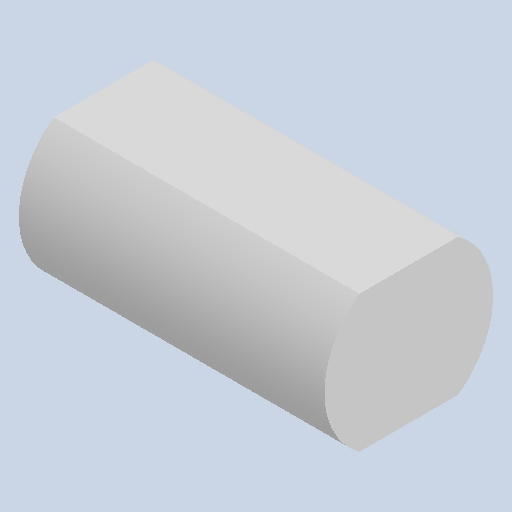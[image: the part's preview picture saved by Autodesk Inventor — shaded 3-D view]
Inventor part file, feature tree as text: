
AUTODESK INVENTOR PART (.ipt)
format: ipt  version: 2022 (Build 260153070, 153G)  size: 98,816 bytes
history: native  units: mm
features: other x3, extrude x1, sketch x1, reference x1
ambient origin geometry x8: Origin, YZ Plane, XZ Plane, XY Plane, X Axis, Y Axis, Z Axis, Center Point
bodies: Body1 (feature_tree)
feature tree (6):
  extrude  "Extrusion2"  Depth=15.0mm
  sketch  "Sketch1"  dims[d2=18.5mm d3=15.0mm d4=33.5mm d5=0.0mm]
  reference  "Reference1"
  other  "<userpath> laptop\Desktop\SumoBot\sumobotENCODER\MotorEncoderAssembly.iam"
  other  "MotorEncoderAssembly.iam"
  other  "TT motor output:1"
